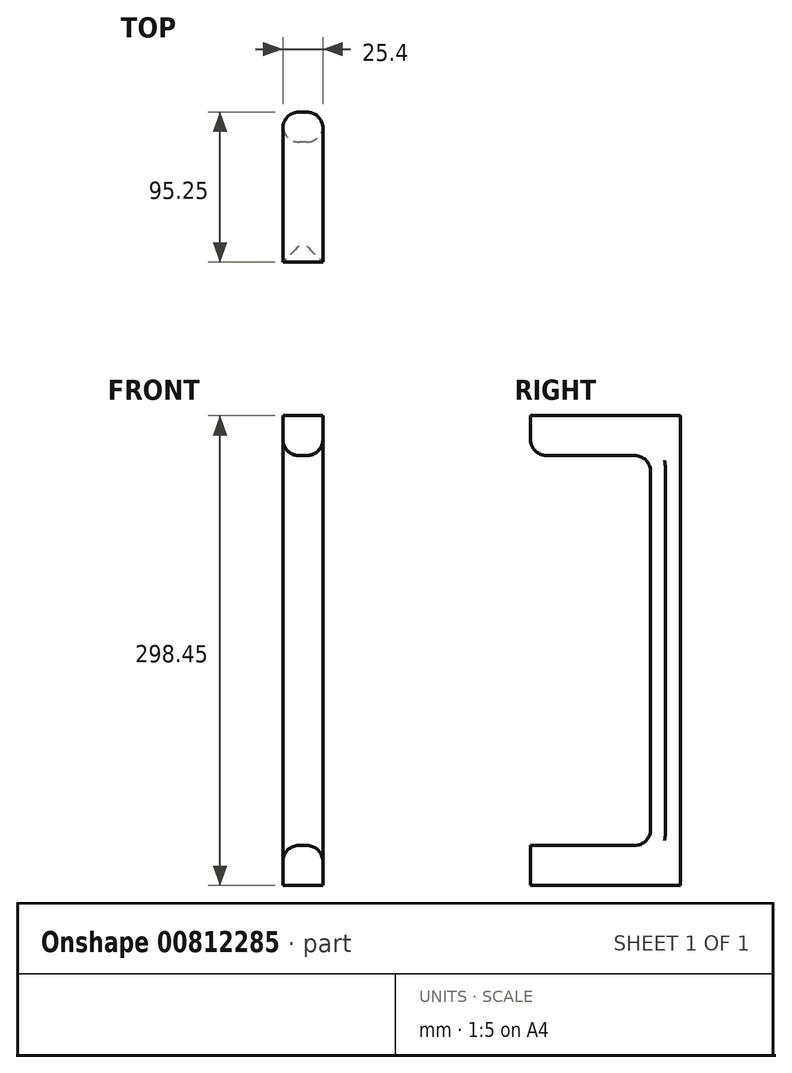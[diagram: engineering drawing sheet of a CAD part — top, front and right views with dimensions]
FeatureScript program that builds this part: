
annotation { "Feature Type Name" : "Feature", "Feature Type Description" : "" }
export const myFeature = defineFeature(function(context is Context, id is Id, definition is map)
    precondition{}
    {
        {
            var Q0;
            Q0=qCreatedBy(makeId("Right.planeOp"),FACE);
            var sketch = newSketch(context, id + "F0", { "sketchPlane" : qUnion([Q0])});
            skLineSegment(sketch, "E0", {"start": v(0, 139.7) * mm, "end": v(0, 0) * mm});
            skLineSegment(sketch, "E1", {"start": v(0, 0) * mm, "end": v(0, 139.7) * mm});
            skLineSegment(sketch, "E2", {"start": v(0, 139.7) * mm, "end": v(19.05, 139.7) * mm});
            skLineSegment(sketch, "E3", {"start": v(19.05, 139.7) * mm, "end": v(19.05, -158.76) * mm});
            skLineSegment(sketch, "E4", {"start": v(19.05, -158.76) * mm, "end": v(-76.2, -158.76) * mm});
            skLineSegment(sketch, "E5", {"start": v(-76.2, -158.76) * mm, "end": v(-76.2, -133.36) * mm});
            skLineSegment(sketch, "E6", {"start": v(-76.2, -133.36) * mm, "end": v(0, -133.36) * mm});
            skLineSegment(sketch, "E7", {"start": v(0, -133.36) * mm, "end": v(0, 0) * mm});
            skLineSegment(sketch, "E8", {"start": v(0, 139.7) * mm, "end": v(-76.2, 139.7) * mm});
            skLineSegment(sketch, "E9", {"start": v(-76.2, 139.7) * mm, "end": v(-76.2, 114.3) * mm});
            skLineSegment(sketch, "E10", {"start": v(-76.2, 114.3) * mm, "end": v(0, 114.3) * mm});
            skSolve(sketch);
        }
        {
            var Q0;
            Q0 = qSketchRegion(id + "F0", true);
            extrude(context, id + "F1", {"entities" : qUnion([Q0]), "depth" : 25.4 * mm, "offsetDistance" : 25.4 * mm});
        }
        {
            var Q0;
            Q0=makeQuery(id+"F1.opExtrude","CAP_EDGE",EDGE,{"disambiguationData":[OSD([sQuery(id+"F0.wireOp",EDGE,"E10")])],"isStart":false});
            var Q1;
            Q1=makeQuery(id+"F1.opExtrude","CAP_EDGE",EDGE,{"disambiguationData":[OSD([sQuery(id+"F0.wireOp",EDGE,"E1"),sQuery(id+"F0.wireOp",EDGE,"E7")])],"isStart":false});
            var Q2;
            Q2=makeQuery(id+"F1.opExtrude","CAP_EDGE",EDGE,{"disambiguationData":[OSD([sQuery(id+"F0.wireOp",EDGE,"E6")])],"isStart":false});
            var Q3;
            Q3=makeQuery(id+"F1.opExtrude","CAP_EDGE",EDGE,{"disambiguationData":[OSD([sQuery(id+"F0.wireOp",EDGE,"E6")])],"isStart":true});
            var Q4;
            Q4=makeQuery(id+"F1.opExtrude","CAP_EDGE",EDGE,{"disambiguationData":[OSD([sQuery(id+"F0.wireOp",EDGE,"E1"),sQuery(id+"F0.wireOp",EDGE,"E7")])],"isStart":true});
            var Q5;
            Q5=makeQuery(id+"F1.opExtrude","CAP_EDGE",EDGE,{"disambiguationData":[OSD([sQuery(id+"F0.wireOp",EDGE,"E3")])],"isStart":true});
            var Q6;
            Q6=makeQuery(id+"F1.opExtrude","CAP_EDGE",EDGE,{"disambiguationData":[OSD([sQuery(id+"F0.wireOp",EDGE,"E10")])],"isStart":true});
            var Q7;
            Q7=makeQuery(id+"F1.opExtrude","SWEPT_EDGE",EDGE,{"disambiguationData":[OSD([sQuery(id+"F0.wireOp",EDGE,"E1"),sQuery(id+"F0.wireOp",EDGE,"E10")])]});
            var Q8;
            Q8=makeQuery(id+"F1.opExtrude","SWEPT_EDGE",EDGE,{"disambiguationData":[OSD([sQuery(id+"F0.wireOp",EDGE,"E6"),sQuery(id+"F0.wireOp",EDGE,"E7")])]});
            var Q9;
            Q9=makeQuery(id+"F1.opExtrude","CAP_EDGE",EDGE,{"disambiguationData":[OSD([sQuery(id+"F0.wireOp",EDGE,"E3")])],"isStart":false});
            fillet(context, id + "F2", {"entities" : qUnion([Q0, Q1, Q2, Q3, Q4, Q5, Q6, Q7, Q8, Q9]), "radius" : 10.16 * mm, "tangentPropagation" : true, "allowEdgeOverflow" : false});
        }
    });
